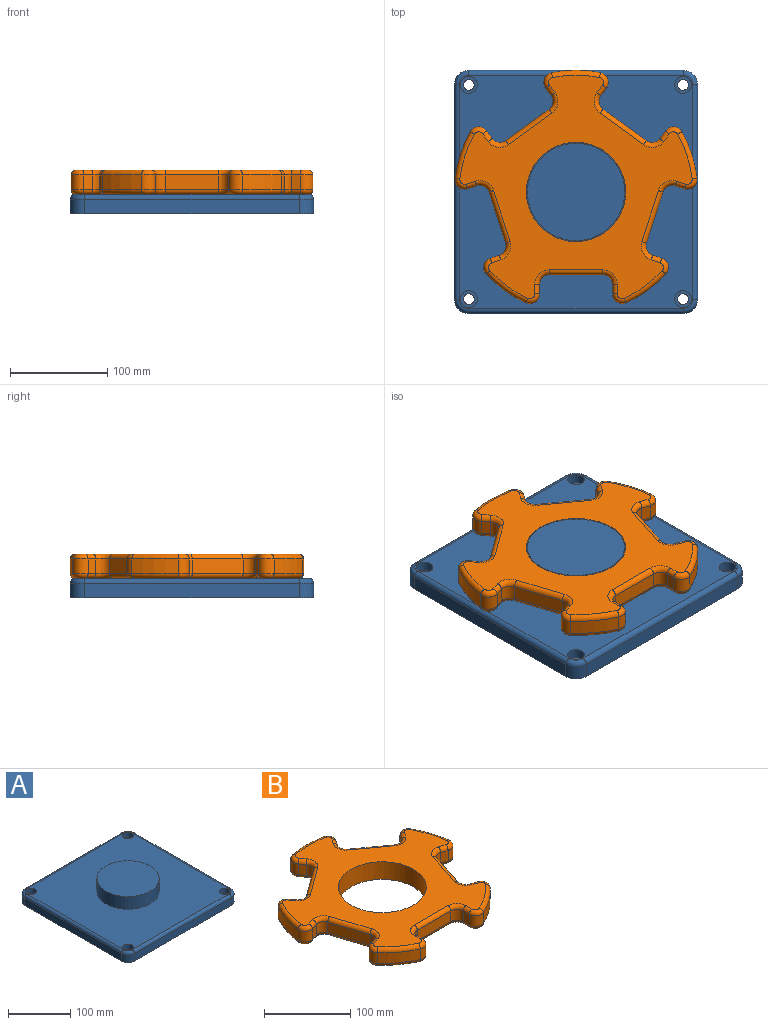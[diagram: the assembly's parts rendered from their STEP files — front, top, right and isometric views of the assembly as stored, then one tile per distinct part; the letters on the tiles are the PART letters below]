
ASSEMBLY  parts=2 mates=1
PART A: 32 faces, bbox 252.5x252.5x45 mm
  f0: plane 220x15mm, normal (1,0,0), area 3300mm2, adj f5,f8,f11,f27
  f1: plane 220x15mm, normal (0,1,0), area 3300mm2, adj f5,f8,f9,f31
  f2: plane 220x15mm, normal (-1,0,0), area 3300mm2, adj f5,f9,f10,f28
  f3: plane 220x15mm, normal (0,-1,0), area 3300mm2, adj f5,f10,f11,f24
  f4: plane 240x240mm, normal (0,0,1), area 48725.4mm2, adj f6,f14,f17,f20,f23,f24,f25,f26
  f5: plane 250x250mm, normal (0,0,-1), area 61926.7mm2, adj f0,f1,f2,f3,f8,f9,f10,f11
  f6: cylinder r=50mm len=100mm, axis (0,0,-1), area 7854mm2, adj f4,f7
  f7: plane 100x100mm, normal (0,0,1), area 7854mm2, adj f6
  f8: cylinder r=15mm len=15mm, axis (0,0,-1), area 353.4mm2, adj f0,f1,f5,f29
  f9: cylinder r=15mm len=15mm, axis (0,0,1), area 353.4mm2, adj f1,f2,f5,f30
  f10: cylinder r=15mm len=15mm, axis (0,0,-1), area 353.4mm2, adj f2,f3,f5,f26
  f11: cylinder r=15mm len=15mm, axis (0,0,1), area 353.4mm2, adj f0,f3,f5,f25
  f12: cylinder r=5.5mm len=11mm, axis (0,0,1), area 345.6mm2, adj f5,f13
  f13: plane 17.25x17.25mm, normal (0,0,1), area 138.7mm2, adj f12,f14
  f14: cylinder r=8.62mm len=17.25mm, axis (0,0,1), area 541.9mm2, adj f4,f13
  f15: cylinder r=5.5mm len=11mm, axis (0,0,1), area 345.6mm2, adj f5,f16
  f16: plane 17.25x17.25mm, normal (0,0,1), area 138.7mm2, adj f15,f17
  f17: cylinder r=8.62mm len=17.25mm, axis (0,0,1), area 541.9mm2, adj f4,f16
  f18: cylinder r=5.5mm len=11mm, axis (0,0,1), area 345.6mm2, adj f5,f19
  f19: plane 17.25x17.25mm, normal (0,0,1), area 138.7mm2, adj f18,f20
  f20: cylinder r=8.62mm len=17.25mm, axis (0,0,1), area 541.9mm2, adj f4,f19
  f21: cylinder r=5.5mm len=11mm, axis (0,0,1), area 345.6mm2, adj f5,f22
  f22: plane 17.25x17.25mm, normal (0,0,1), area 138.7mm2, adj f21,f23
  f23: cylinder r=8.62mm len=17.25mm, axis (0,0,1), area 541.9mm2, adj f4,f22
  f24: cylinder r=5mm len=220mm, axis (-1,0,0), area 1727.9mm2, adj f3,f4,f25,f26
  f25: torus R=10mm, axis (0,0,1), area 162.6mm2, adj f4,f11,f24,f27
  f26: torus R=10mm, axis (0,0,1), area 162.6mm2, adj f4,f10,f24,f28
  f27: cylinder r=5mm len=220mm, axis (0,-1,0), area 1727.9mm2, adj f0,f4,f25,f29
  f28: cylinder r=5mm len=220mm, axis (0,1,0), area 1727.9mm2, adj f2,f4,f26,f30
  f29: torus R=10mm, axis (0,0,1), area 162.6mm2, adj f4,f8,f27,f31
  f30: torus R=10mm, axis (0,0,1), area 162.6mm2, adj f4,f9,f28,f31
  f31: cylinder r=5mm len=220mm, axis (1,0,0), area 1727.9mm2, adj f1,f4,f29,f30
PART B: 123 faces, bbox 268.9x258.5x25 mm
  f0: plane 238.57x229.73mm, normal (0,0,1), area 21505.7mm2, adj f6,f83,f84,f85,f86,f87,f88,f89
  f1: plane 238.57x229.73mm, normal (0,0,-1), area 21505.7mm2, adj f6,f43,f44,f45,f46,f47,f48,f49
  f2: cylinder r=125mm len=47.82mm, axis (0,0,-1), area 759.5mm2, adj f34,f42,f74,f114
  f3: cylinder r=125mm len=50.29mm, axis (0,0,-1), area 759.5mm2, adj f27,f35,f75,f115
  f4: cylinder r=125mm len=47.82mm, axis (0,0,-1), area 759.5mm2, adj f20,f28,f59,f99
  f5: cylinder r=125mm len=40.68mm, axis (0,0,-1), area 759.5mm2, adj f13,f21,f43,f83
  f6: cylinder r=51mm len=102mm, axis (0,0,-1), area 8011.1mm2, adj f0,f1
  f7: cylinder r=125mm len=40.68mm, axis (0,0,-1), area 759.5mm2, adj f14,f41,f58,f98
  f8: plane 15x9.73mm, normal (-1,0,0), area 146mm2, adj f11,f14,f54,f94
  f9: plane 55x15mm, normal (0,-1,0), area 825mm2, adj f11,f12,f50,f90
  f10: plane 15x9.73mm, normal (1,0,0), area 146mm2, adj f12,f13,f46,f86
  f11: cylinder r=10mm len=15mm, axis (0,0,-1), area 235.6mm2, adj f8,f9,f52,f92
  f12: cylinder r=10mm len=15mm, axis (0,0,-1), area 235.6mm2, adj f9,f10,f48,f88
  f13: cylinder r=10mm len=15mm, axis (0,0,-1), area 299.5mm2, adj f5,f10,f44,f84
  f14: cylinder r=10mm len=15mm, axis (0,0,-1), area 299.5mm2, adj f7,f8,f56,f96
  f15: plane 15x9.26mm, normal (-0.31,0.95,0), area 146mm2, adj f18,f21,f47,f87
  f16: plane 52.31x17mm, normal (-0.95,-0.31,0), area 825mm2, adj f18,f19,f51,f91
  f17: plane 15x9.26mm, normal (0.31,-0.95,0), area 146mm2, adj f19,f20,f55,f95
  f18: cylinder r=10mm len=15mm, axis (0,0,-1), area 235.6mm2, adj f15,f16,f49,f89
  f19: cylinder r=10mm len=15mm, axis (0,0,-1), area 235.6mm2, adj f16,f17,f53,f93
  f20: cylinder r=10mm len=15mm, axis (0,0,-1), area 299.5mm2, adj f4,f17,f57,f97
  f21: cylinder r=10mm len=16.25mm, axis (0,0,-1), area 299.5mm2, adj f5,f15,f45,f85
  f22: plane 15x7.87mm, normal (0.81,0.59,0), area 146mm2, adj f25,f28,f63,f103
  f23: plane 44.5x32.33mm, normal (-0.59,0.81,0), area 825mm2, adj f25,f26,f67,f107
  f24: plane 15x7.87mm, normal (-0.81,-0.59,0), area 146mm2, adj f26,f27,f71,f111
  f25: cylinder r=10mm len=15mm, axis (0,0,-1), area 235.6mm2, adj f22,f23,f65,f105
  f26: cylinder r=10mm len=15mm, axis (0,0,-1), area 235.6mm2, adj f23,f24,f69,f109
  f27: cylinder r=10mm len=15.67mm, axis (0,0,-1), area 299.5mm2, adj f3,f24,f73,f113
  f28: cylinder r=10mm len=16.78mm, axis (0,0,-1), area 299.5mm2, adj f4,f22,f61,f101
  f29: plane 15x7.87mm, normal (0.81,-0.59,0), area 146mm2, adj f32,f35,f79,f119
  f30: plane 44.5x32.33mm, normal (0.59,0.81,0), area 825mm2, adj f32,f33,f82,f122
  f31: plane 15x7.87mm, normal (-0.81,0.59,0), area 146mm2, adj f33,f34,f78,f118
  f32: cylinder r=10mm len=15mm, axis (0,0,-1), area 235.6mm2, adj f29,f30,f81,f121
  f33: cylinder r=10mm len=15mm, axis (0,0,-1), area 235.6mm2, adj f30,f31,f80,f120
  f34: cylinder r=10mm len=16.78mm, axis (0,0,-1), area 299.5mm2, adj f2,f31,f76,f116
  f35: cylinder r=10mm len=15.67mm, axis (0,0,-1), area 299.5mm2, adj f3,f29,f77,f117
  f36: plane 15x9.26mm, normal (-0.31,-0.95,0), area 146mm2, adj f39,f42,f70,f110
  f37: plane 52.31x17mm, normal (0.95,-0.31,0), area 825mm2, adj f39,f40,f66,f106
  f38: plane 15x9.26mm, normal (0.31,0.95,0), area 146mm2, adj f40,f41,f62,f102
  f39: cylinder r=10mm len=15mm, axis (0,0,-1), area 235.6mm2, adj f36,f37,f68,f108
  f40: cylinder r=10mm len=15mm, axis (0,0,-1), area 235.6mm2, adj f37,f38,f64,f104
  f41: cylinder r=10mm len=16.25mm, axis (0,0,-1), area 299.5mm2, adj f7,f38,f60,f100
  f42: cylinder r=10mm len=15mm, axis (0,0,-1), area 299.5mm2, adj f2,f36,f72,f112
  f43: torus R=120mm, axis (0,0,1), area 391.9mm2, adj f1,f5,f44,f45
  f44: torus R=5mm, axis (0,0,1), area 128.3mm2, adj f1,f13,f43,f46
  f45: torus R=5mm, axis (0,0,1), area 128.3mm2, adj f1,f21,f43,f47
  f46: cylinder r=5mm len=9.73mm, axis (0,-1,0), area 76.4mm2, adj f1,f10,f44,f48
  f47: cylinder r=5mm len=10.8mm, axis (0.95,0.31,0), area 76.4mm2, adj f1,f15,f45,f49
  f48: torus R=15mm, axis (0,0,1), area 145.8mm2, adj f1,f12,f46,f50
  f49: torus R=15mm, axis (0,0,1), area 145.8mm2, adj f1,f18,f47,f51
  f50: cylinder r=5mm len=55mm, axis (-1,0,0), area 432mm2, adj f1,f9,f48,f52
  f51: cylinder r=5mm len=53.85mm, axis (-0.31,0.95,0), area 432mm2, adj f1,f16,f49,f53
  f52: torus R=15mm, axis (0,0,1), area 145.8mm2, adj f1,f11,f50,f54
  f53: torus R=15mm, axis (0,0,1), area 145.8mm2, adj f1,f19,f51,f55
  f54: cylinder r=5mm len=9.73mm, axis (0,1,0), area 76.4mm2, adj f1,f8,f52,f56
  f55: cylinder r=5mm len=10.8mm, axis (-0.95,-0.31,0), area 76.4mm2, adj f1,f17,f53,f57
  f56: torus R=5mm, axis (0,0,1), area 128.3mm2, adj f1,f14,f54,f58
  f57: torus R=5mm, axis (0,0,1), area 128.3mm2, adj f1,f20,f55,f59
  f58: torus R=120mm, axis (0,0,1), area 391.9mm2, adj f1,f7,f56,f60
  f59: torus R=120mm, axis (0,0,1), area 391.9mm2, adj f1,f4,f57,f61
  f60: torus R=5mm, axis (0,0,1), area 128.3mm2, adj f1,f41,f58,f62
  f61: torus R=5mm, axis (0,0,1), area 128.3mm2, adj f1,f28,f59,f63
  f62: cylinder r=5mm len=10.8mm, axis (0.95,-0.31,0), area 76.4mm2, adj f1,f38,f60,f64
  f63: cylinder r=5mm len=10.81mm, axis (0.59,-0.81,0), area 76.4mm2, adj f1,f22,f61,f65
  f64: torus R=15mm, axis (0,0,1), area 145.8mm2, adj f1,f40,f62,f66
  f65: torus R=15mm, axis (0,0,1), area 145.8mm2, adj f1,f25,f63,f67
  f66: cylinder r=5mm len=53.85mm, axis (-0.31,-0.95,0), area 432mm2, adj f1,f37,f64,f68
  f67: cylinder r=5mm len=47.44mm, axis (0.81,0.59,0), area 432mm2, adj f1,f23,f65,f69
  f68: torus R=15mm, axis (0,0,1), area 145.8mm2, adj f1,f39,f66,f70
  f69: torus R=15mm, axis (0,0,1), area 145.8mm2, adj f1,f26,f67,f71
  f70: cylinder r=5mm len=10.8mm, axis (-0.95,0.31,0), area 76.4mm2, adj f1,f36,f68,f72
  f71: cylinder r=5mm len=10.81mm, axis (-0.59,0.81,0), area 76.4mm2, adj f1,f24,f69,f73
  f72: torus R=5mm, axis (0,0,1), area 128.3mm2, adj f1,f42,f70,f74
  f73: torus R=5mm, axis (0,0,1), area 128.3mm2, adj f1,f27,f71,f75
  f74: torus R=120mm, axis (0,0,1), area 391.9mm2, adj f1,f2,f72,f76
  f75: torus R=120mm, axis (0,0,1), area 391.9mm2, adj f1,f3,f73,f77
  f76: torus R=5mm, axis (0,0,1), area 128.3mm2, adj f1,f34,f74,f78
  f77: torus R=5mm, axis (0,0,1), area 128.3mm2, adj f1,f35,f75,f79
  f78: cylinder r=5mm len=10.81mm, axis (0.59,0.81,0), area 76.4mm2, adj f1,f31,f76,f80
  f79: cylinder r=5mm len=10.81mm, axis (-0.59,-0.81,0), area 76.4mm2, adj f1,f29,f77,f81
  f80: torus R=15mm, axis (0,0,1), area 145.8mm2, adj f1,f33,f78,f82
  f81: torus R=15mm, axis (0,0,1), area 145.8mm2, adj f1,f32,f79,f82
  f82: cylinder r=5mm len=47.44mm, axis (0.81,-0.59,0), area 432mm2, adj f1,f30,f80,f81
  f83: torus R=120mm, axis (0,0,1), area 391.9mm2, adj f0,f5,f84,f85
  f84: torus R=5mm, axis (0,0,1), area 128.3mm2, adj f0,f13,f83,f86
  f85: torus R=5mm, axis (0,0,1), area 128.3mm2, adj f0,f21,f83,f87
  f86: cylinder r=5mm len=9.73mm, axis (0,1,0), area 76.4mm2, adj f0,f10,f84,f88
  f87: cylinder r=5mm len=10.8mm, axis (-0.95,-0.31,0), area 76.4mm2, adj f0,f15,f85,f89
  f88: torus R=15mm, axis (0,0,1), area 145.8mm2, adj f0,f12,f86,f90
  f89: torus R=15mm, axis (0,0,1), area 145.8mm2, adj f0,f18,f87,f91
  f90: cylinder r=5mm len=55mm, axis (1,0,0), area 432mm2, adj f0,f9,f88,f92
  f91: cylinder r=5mm len=53.85mm, axis (0.31,-0.95,0), area 432mm2, adj f0,f16,f89,f93
  f92: torus R=15mm, axis (0,0,1), area 145.8mm2, adj f0,f11,f90,f94
  f93: torus R=15mm, axis (0,0,1), area 145.8mm2, adj f0,f19,f91,f95
  f94: cylinder r=5mm len=9.73mm, axis (0,-1,0), area 76.4mm2, adj f0,f8,f92,f96
  f95: cylinder r=5mm len=10.8mm, axis (0.95,0.31,0), area 76.4mm2, adj f0,f17,f93,f97
  f96: torus R=5mm, axis (0,0,1), area 128.3mm2, adj f0,f14,f94,f98
  f97: torus R=5mm, axis (0,0,1), area 128.3mm2, adj f0,f20,f95,f99
  f98: torus R=120mm, axis (0,0,1), area 391.9mm2, adj f0,f7,f96,f100
  f99: torus R=120mm, axis (0,0,1), area 391.9mm2, adj f0,f4,f97,f101
  f100: torus R=5mm, axis (0,0,1), area 128.3mm2, adj f0,f41,f98,f102
  f101: torus R=5mm, axis (0,0,1), area 128.3mm2, adj f0,f28,f99,f103
  f102: cylinder r=5mm len=10.8mm, axis (-0.95,0.31,0), area 76.4mm2, adj f0,f38,f100,f104
  f103: cylinder r=5mm len=10.81mm, axis (-0.59,0.81,0), area 76.4mm2, adj f0,f22,f101,f105
  f104: torus R=15mm, axis (0,0,1), area 145.8mm2, adj f0,f40,f102,f106
  f105: torus R=15mm, axis (0,0,1), area 145.8mm2, adj f0,f25,f103,f107
  f106: cylinder r=5mm len=53.85mm, axis (0.31,0.95,0), area 432mm2, adj f0,f37,f104,f108
  f107: cylinder r=5mm len=47.44mm, axis (-0.81,-0.59,0), area 432mm2, adj f0,f23,f105,f109
  f108: torus R=15mm, axis (0,0,1), area 145.8mm2, adj f0,f39,f106,f110
  f109: torus R=15mm, axis (0,0,1), area 145.8mm2, adj f0,f26,f107,f111
  f110: cylinder r=5mm len=10.8mm, axis (0.95,-0.31,0), area 76.4mm2, adj f0,f36,f108,f112
  f111: cylinder r=5mm len=10.81mm, axis (0.59,-0.81,0), area 76.4mm2, adj f0,f24,f109,f113
  f112: torus R=5mm, axis (0,0,1), area 128.3mm2, adj f0,f42,f110,f114
  f113: torus R=5mm, axis (0,0,1), area 128.3mm2, adj f0,f27,f111,f115
  f114: torus R=120mm, axis (0,0,1), area 391.9mm2, adj f0,f2,f112,f116
  f115: torus R=120mm, axis (0,0,1), area 391.9mm2, adj f0,f3,f113,f117
  f116: torus R=5mm, axis (0,0,1), area 128.3mm2, adj f0,f34,f114,f118
  f117: torus R=5mm, axis (0,0,1), area 128.3mm2, adj f0,f35,f115,f119
  f118: cylinder r=5mm len=10.81mm, axis (-0.59,-0.81,0), area 76.4mm2, adj f0,f31,f116,f120
  f119: cylinder r=5mm len=10.81mm, axis (0.59,0.81,0), area 76.4mm2, adj f0,f29,f117,f121
  f120: torus R=15mm, axis (0,0,1), area 145.8mm2, adj f0,f33,f118,f122
  f121: torus R=15mm, axis (0,0,1), area 145.8mm2, adj f0,f32,f119,f122
  f122: cylinder r=5mm len=47.44mm, axis (-0.81,0.59,0), area 432mm2, adj f0,f30,f120,f121
PLACE A at identity fixed
PLACE B at identity
MATE revolute B.f2 <-> A.f6  axis (0,0,-1) through (0,0,20)mm
